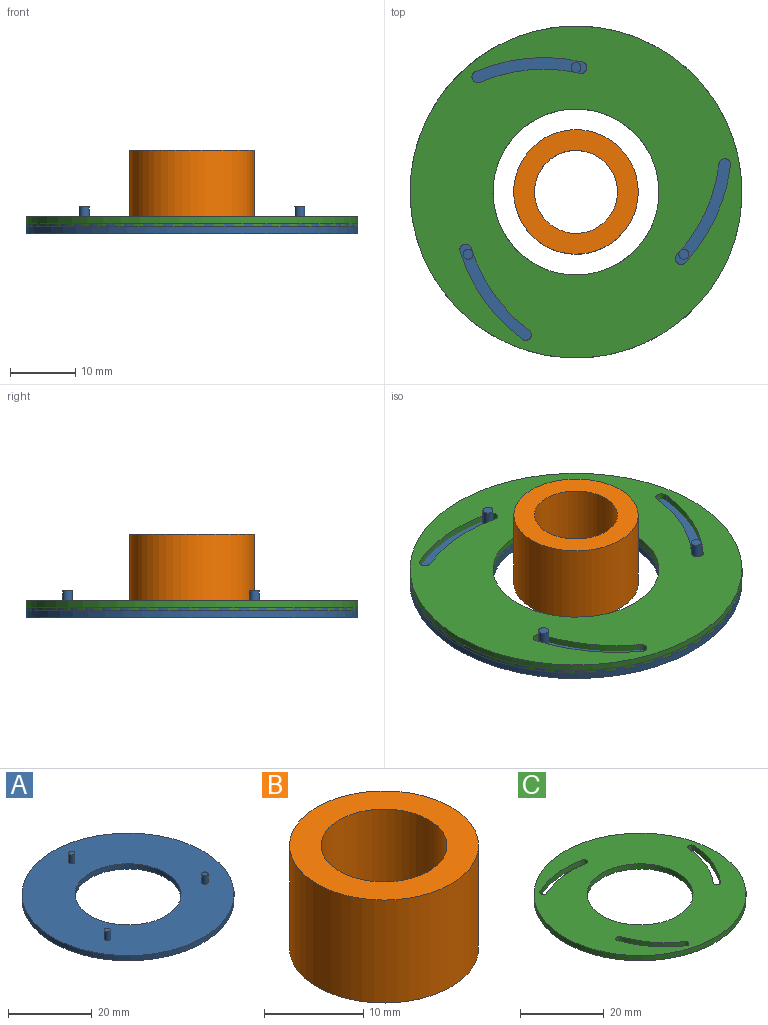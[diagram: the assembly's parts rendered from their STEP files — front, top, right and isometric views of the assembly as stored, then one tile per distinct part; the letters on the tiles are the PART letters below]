
ASSEMBLY  parts=3 mates=2
PART A: 10 faces, bbox 50.8x50.8x4.1 mm
  f0: cylinder r=12.7mm len=25.4mm, axis (0,0,-1), area 121.6mm2, adj f2,f3
  f1: cylinder r=25.4mm len=50.8mm, axis (0,0,-1), area 243.2mm2, adj f2,f3
  f2: plane 50.8x50.8mm, normal (0,0,1), area 1514.6mm2, adj f0,f1,f4,f6,f8
  f3: plane 50.8x50.8mm, normal (0,0,-1), area 1520.1mm2, adj f0,f1
  f4: cylinder r=0.76mm len=2.54mm, axis (0,0,-1), area 12.2mm2, adj f2,f5
  f5: plane 1.52x1.52mm, normal (0,0,1), area 1.8mm2, adj f4
  f6: cylinder r=0.76mm len=2.54mm, axis (0,0,-1), area 12.2mm2, adj f2,f7
  f7: plane 1.52x1.52mm, normal (0,0,1), area 1.8mm2, adj f6
  f8: cylinder r=0.76mm len=2.54mm, axis (0,0,-1), area 12.2mm2, adj f2,f9
  f9: plane 1.52x1.52mm, normal (0,0,1), area 1.8mm2, adj f8
PART B: 4 faces, bbox 19.1x19.1x12.7 mm
  f0: cylinder r=6.35mm len=12.7mm, axis (0,0,-1), area 506.7mm2, adj f2,f3
  f1: cylinder r=9.53mm len=19.05mm, axis (0,0,-1), area 760.1mm2, adj f2,f3
  f2: plane 19.05x19.05mm, normal (0,0,1), area 158.3mm2, adj f0,f1
  f3: plane 19.05x19.05mm, normal (0,0,-1), area 158.3mm2, adj f0,f1
PART C: 16 faces, bbox 50.8x50.8x1.5 mm
  f0: plane 50.8x50.8mm, normal (0,0,1), area 1426.6mm2, adj f2,f3,f4,f5,f6,f7,f8,f9
  f1: plane 50.8x50.8mm, normal (0,0,-1), area 1426.6mm2, adj f2,f3,f4,f5,f6,f7,f8,f9
  f2: cylinder r=12.7mm len=25.4mm, axis (0,0,-1), area 121.6mm2, adj f0,f1
  f3: cylinder r=25.4mm len=50.8mm, axis (0,0,-1), area 243.2mm2, adj f0,f1
  f4: cylinder r=24.51mm len=12.15mm, axis (0,0,1), area 23.7mm2, adj f0,f1,f5,f7
  f5: cylinder r=0.89mm len=1.73mm, axis (0,0,1), area 4.3mm2, adj f0,f1,f4,f6
  f6: cylinder r=26.29mm len=13.03mm, axis (0,0,1), area 25.5mm2, adj f0,f1,f5,f7
  f7: cylinder r=0.89mm len=1.62mm, axis (0,0,1), area 4.3mm2, adj f0,f1,f4,f6
  f8: cylinder r=0.89mm len=1.56mm, axis (0,0,1), area 4.3mm2, adj f0,f1,f9,f11
  f9: cylinder r=26.29mm len=15.18mm, axis (0,0,1), area 25.5mm2, adj f0,f1,f8,f10
  f10: cylinder r=0.89mm len=1.78mm, axis (0,0,1), area 4.3mm2, adj f0,f1,f9,f11
  f11: cylinder r=24.51mm len=14.16mm, axis (0,0,1), area 23.7mm2, adj f0,f1,f8,f10
  f12: cylinder r=0.89mm len=1.69mm, axis (0,0,1), area 4.3mm2, adj f0,f1,f13,f15
  f13: cylinder r=24.51mm len=15.19mm, axis (0,0,1), area 23.7mm2, adj f0,f1,f12,f14
  f14: cylinder r=0.89mm len=1.76mm, axis (0,0,1), area 4.3mm2, adj f0,f1,f13,f15
  f15: cylinder r=26.29mm len=16.29mm, axis (0,0,1), area 25.5mm2, adj f0,f1,f12,f14
PLACE A at identity
PLACE B at identity
PLACE C rot(axis=(0,0,1),117.7deg) t=(0,0,1.02)mm
MATE revolute A.f1 <-> C.f3  axis (0,0,-1) through (0,0,0)mm
MATE fastened B.f0 <-> A.f0  axis (0,0,-1) through (0,0,0)mm
